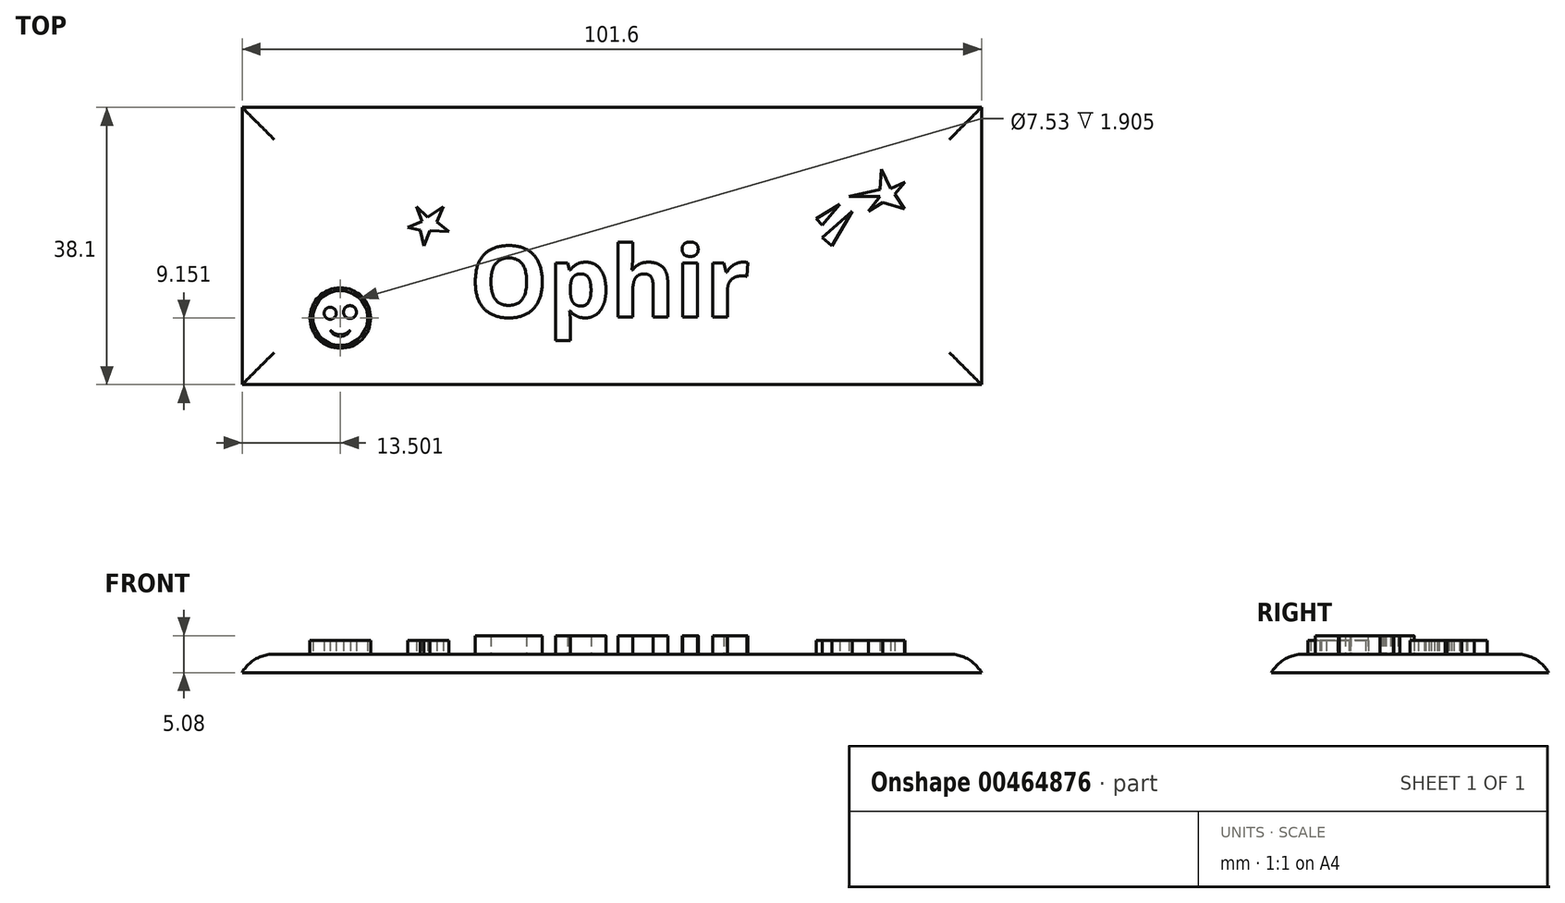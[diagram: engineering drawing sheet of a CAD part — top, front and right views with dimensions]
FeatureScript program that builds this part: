
annotation { "Feature Type Name" : "Feature", "Feature Type Description" : "" }
export const myFeature = defineFeature(function(context is Context, id is Id, definition is map)
    precondition{}
    {
        {
            var Q0;
            Q0=qCreatedBy(makeId("Top.planeOp"),FACE);
            var sketch = newSketch(context, id + "F0", { "sketchPlane" : qUnion([Q0])});
            skLineSegment(sketch, "E0.bottom", {"start": v(50.8, 19.05) * mm, "end": v(-50.8, 19.05) * mm});
            skLineSegment(sketch, "E0.top", {"start": v(50.8, -19.05) * mm, "end": v(-50.8, -19.05) * mm});
            skLineSegment(sketch, "E0.left", {"start": v(50.8, 19.05) * mm, "end": v(50.8, -19.05) * mm});
            skLineSegment(sketch, "E0.right", {"start": v(-50.8, 19.05) * mm, "end": v(-50.8, -19.05) * mm});
            skPoint(sketch, "E0.middle", {"position": v(0, 0) * mm});
            skSolve(sketch);
        }
        {
            var Q0;
            Q0=makeQuery(id+"F0.imprint","IMPRINT",FACE,{"disambiguationData":[TD([[makeQuery(id+"F0.imprint","IMPRINT",EDGE,{"derivedFrom":sQuery(id+"F0.wireOp",EDGE,"E0.bottom")}),1.0]])]});
            extrude(context, id + "F1", {"entities" : qUnion([Q0]), "depth" : 2.54 * mm});
        }
        {
            var Q0;
            Q0=makeQuery(id+"F1.opExtrude","CAP_FACE",FACE,{"disambiguationData":[OSD([sQuery(id+"F0.wireOp",EDGE,"E0.bottom"),sQuery(id+"F0.wireOp",EDGE,"E0.top"),sQuery(id+"F0.wireOp",EDGE,"E0.left"),sQuery(id+"F0.wireOp",EDGE,"E0.right")])],"isStart":false});
            var sketch = newSketch(context, id + "F2", { "sketchPlane" : qUnion([Q0])});
            skText(sketch, "E1", { "text": "Ophir", "fontName": "NotoSans-Bold.ttf"});
            skLineSegment(sketch, "E2", {"start": v(-19.54, 0) * mm, "end": v(19.58, 0) * mm, "construction": true});
            skPoint(sketch, "E3", {"position": v(0.02, 0) * mm});
            const initialGuessF2  = {"E1": [-0.01954, -0.00975, 1, 0, 0.00975]};
            skSetInitialGuess(sketch, initialGuessF2);
            skSolve(sketch);
        }
        {
            var Q0;
            Q0 = qSketchRegion(id + "F2", true);
            extrude(context, id + "F3", {"entities" : qUnion([Q0]), "operationType" : NewBodyOperationType.ADD, "depth" : 2.54 * mm});
        }
        {
            var Q0;
            Q0=makeQuery(id+"F1.opExtrude","CAP_EDGE",EDGE,{"disambiguationData":[OSD([sQuery(id+"F0.wireOp",EDGE,"E0.bottom")])],"isStart":false});
            var Q1;
            Q1=makeQuery(id+"F1.opExtrude","CAP_EDGE",EDGE,{"disambiguationData":[OSD([sQuery(id+"F0.wireOp",EDGE,"E0.right")])],"isStart":false});
            var Q2;
            Q2=makeQuery(id+"F1.opExtrude","CAP_EDGE",EDGE,{"disambiguationData":[OSD([sQuery(id+"F0.wireOp",EDGE,"E0.top")])],"isStart":false});
            var Q3;
            Q3=makeQuery(id+"F1.opExtrude","CAP_EDGE",EDGE,{"disambiguationData":[OSD([sQuery(id+"F0.wireOp",EDGE,"E0.left")])],"isStart":false});
            fillet(context, id + "F4", {"entities" : qUnion([Q0, Q1, Q2, Q3]), "radius" : 5.08 * mm, "tangentPropagation" : true, "allowEdgeOverflow" : false});
        }
        {
            var Q0;
            {var subQ0=sQuery(id+"F0.wireOp",EDGE,"E0.left");var subQ1=sQuery(id+"F0.wireOp",EDGE,"E0.bottom");var subQ2=sQuery(id+"F0.wireOp",EDGE,"E0.right");var subQ3=sQuery(id+"F0.wireOp",EDGE,"E0.top");Q0=makeQuery(id+"F3.boolean.opBoolean","SPLIT",FACE,{"disambiguationData":[TD([makeQuery(id+"F1.opExtrude","SWEPT_FACE",FACE,{"disambiguationData":[OSD([subQ1])]})])],"derivedFrom":makeQuery(id+"F1.opExtrude","CAP_FACE",FACE,{"disambiguationData":[OSD([subQ1,subQ3,subQ0,subQ2])],"isStart":false})});}
            var sketch = newSketch(context, id + "F5", { "sketchPlane" : qUnion([Q0])});
            skLineSegment(sketch, "E4", {"start": v(-26.1, 3.38) * mm, "end": v(-26.84, 5.4) * mm});
            skLineSegment(sketch, "E5", {"start": v(-26.84, 5.4) * mm, "end": v(-25.29, 3.99) * mm});
            skLineSegment(sketch, "E6", {"start": v(-25.29, 3.99) * mm, "end": v(-23.14, 5.4) * mm});
            skLineSegment(sketch, "E7", {"start": v(-23.14, 5.4) * mm, "end": v(-24.01, 3.32) * mm});
            skLineSegment(sketch, "E8", {"start": v(-24.01, 3.32) * mm, "end": v(-22.39, 1.98) * mm});
            skLineSegment(sketch, "E9", {"start": v(-22.39, 1.98) * mm, "end": v(-25.01, 2.1) * mm});
            skLineSegment(sketch, "E10", {"start": v(-25.01, 2.1) * mm, "end": v(-25.8, 0) * mm});
            skLineSegment(sketch, "E11", {"start": v(-25.8, 0) * mm, "end": v(-26.3, 2.17) * mm});
            skLineSegment(sketch, "E12", {"start": v(-26.3, 2.17) * mm, "end": v(-28.04, 2.57) * mm});
            skLineSegment(sketch, "E13", {"start": v(-28.04, 2.57) * mm, "end": v(-26.1, 3.38) * mm});
            skLineSegment(sketch, "E14", {"start": v(36.88, 7.75) * mm, "end": v(37.07, 10.57) * mm});
            skLineSegment(sketch, "E15", {"start": v(37.07, 10.57) * mm, "end": v(38.31, 7.88) * mm});
            skLineSegment(sketch, "E16", {"start": v(38.31, 7.88) * mm, "end": v(40.3, 8.79) * mm});
            skLineSegment(sketch, "E17", {"start": v(40.3, 8.79) * mm, "end": v(38.89, 7.13) * mm});
            skLineSegment(sketch, "E18", {"start": v(38.89, 7.13) * mm, "end": v(40.25, 5.07) * mm});
            skLineSegment(sketch, "E19", {"start": v(40.25, 5.07) * mm, "end": v(37.22, 6) * mm});
            skLineSegment(sketch, "E20", {"start": v(37.22, 6) * mm, "end": v(35.28, 4.79) * mm});
            skLineSegment(sketch, "E21", {"start": v(35.28, 4.79) * mm, "end": v(36.88, 6.8) * mm});
            skLineSegment(sketch, "E22", {"start": v(36.88, 6.8) * mm, "end": v(32.6, 6.8) * mm});
            skLineSegment(sketch, "E23", {"start": v(32.6, 6.8) * mm, "end": v(36.88, 7.75) * mm});
            skLineSegment(sketch, "E24", {"start": v(28.1, 3.76) * mm, "end": v(31.31, 5.72) * mm});
            skLineSegment(sketch, "E25", {"start": v(31.31, 5.72) * mm, "end": v(28.9, 2.89) * mm});
            skLineSegment(sketch, "E26", {"start": v(28.9, 2.89) * mm, "end": v(28.1, 3.76) * mm});
            skLineSegment(sketch, "E27", {"start": v(33.06, 4.79) * mm, "end": v(28.9, 1.14) * mm});
            skLineSegment(sketch, "E28", {"start": v(28.9, 1.14) * mm, "end": v(30.24, 0) * mm});
            skLineSegment(sketch, "E29", {"start": v(30.24, 0) * mm, "end": v(33.06, 4.79) * mm});
            skCircle(sketch, "E30", {"center": v(-37.3, -9.9) * mm, "radius": 3.76 * mm});
            skCircle(sketch, "E31", {"center": v(-38.7, -9.24) * mm, "radius": 0.83 * mm});
            skCircle(sketch, "E32", {"center": v(-35.97, -9.09) * mm, "radius": 0.89 * mm});
            skArc(sketch, "E33", {"start": v(-38.7, -11.52) * mm, "mid": v(-37.26, -12.4) * mm, "end": v(-35.87, -11.45) * mm});
            skArc(sketch, "E34", {"start": v(-38.7, -11.52) * mm, "mid": v(-37.3, -12.2) * mm, "end": v(-35.9, -11.52) * mm});
            skCircle(sketch, "E35", {"center": v(-37.3, -9.9) * mm, "radius": 4.17 * mm});
            skSolve(sketch);
        }
        {
            var Q0;
            Q0=makeQuery(id+"F5.imprint","IMPRINT",FACE,{"disambiguationData":[TD([[makeQuery(id+"F5.imprint","IMPRINT",EDGE,{"derivedFrom":sQuery(id+"F5.wireOp",EDGE,"E4")}),-1.0]])]});
            var Q1;
            Q1=makeQuery(id+"F5.imprint","IMPRINT",FACE,{"disambiguationData":[TD([[makeQuery(id+"F5.imprint","IMPRINT",EDGE,{"derivedFrom":sQuery(id+"F5.wireOp",EDGE,"E14")}),-1.0]])]});
            var Q2;
            Q2=makeQuery(id+"F5.imprint","IMPRINT",FACE,{"disambiguationData":[TD([[makeQuery(id+"F5.imprint","IMPRINT",EDGE,{"derivedFrom":sQuery(id+"F5.wireOp",EDGE,"E27")}),1.0]])]});
            var Q3;
            Q3=makeQuery(id+"F5.imprint","IMPRINT",FACE,{"disambiguationData":[TD([[makeQuery(id+"F5.imprint","IMPRINT",EDGE,{"derivedFrom":sQuery(id+"F5.wireOp",EDGE,"E24")}),-1.0]])]});
            var Q4;
            Q4=makeQuery(id+"F5.imprint","IMPRINT",FACE,{"disambiguationData":[TD([[makeQuery(id+"F5.imprint","IMPRINT",EDGE,{"derivedFrom":sQuery(id+"F5.wireOp",EDGE,"E32")}),1.0]])]});
            var Q5;
            Q5=makeQuery(id+"F5.imprint","IMPRINT",FACE,{"disambiguationData":[TD([[makeQuery(id+"F5.imprint","IMPRINT",EDGE,{"derivedFrom":sQuery(id+"F5.wireOp",EDGE,"E31")}),1.0]])]});
            var Q6;
            {var subQ0=sQuery(id+"F5.wireOp",EDGE,"E34");Q6=makeQuery(id+"F5.imprint","IMPRINT",FACE,{"disambiguationData":[TD([[makeQuery(id+"F5.imprint","IMPRINT",EDGE,{"derivedFrom":subQ0}),-1.0]])]});}
            var Q7;
            Q7=makeQuery(id+"F5.imprint","IMPRINT",FACE,{"disambiguationData":[TD([[makeQuery(id+"F5.imprint","IMPRINT",EDGE,{"derivedFrom":sQuery(id+"F5.wireOp",EDGE,"E30")}),-1.0]])]});
            extrude(context, id + "F6", {"entities" : qUnion([Q0, Q1, Q2, Q3, Q4, Q5, Q6, Q7]), "operationType" : NewBodyOperationType.ADD, "depth" : 1.9 * mm});
        }
    });
